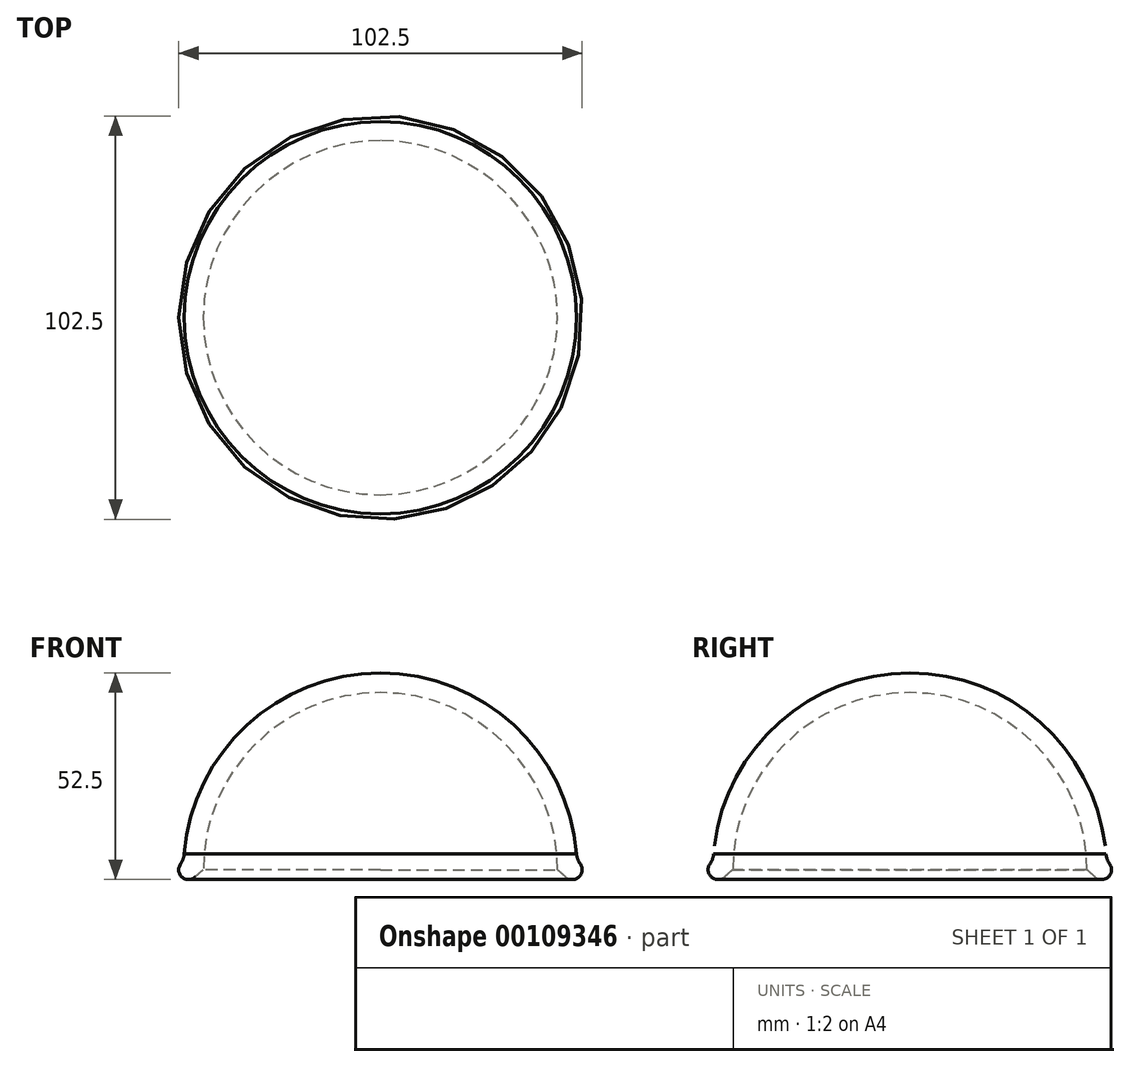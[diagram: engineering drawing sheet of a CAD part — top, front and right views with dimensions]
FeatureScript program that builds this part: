
annotation { "Feature Type Name" : "Feature", "Feature Type Description" : "" }
export const myFeature = defineFeature(function(context is Context, id is Id, definition is map)
    precondition{}
    {
        {
            var Q0;
            Q0=qCreatedBy(makeId("Top.planeOp"),FACE);
            var sketch = newSketch(context, id + "F0", { "sketchPlane" : qUnion([Q0])});
            skCircle(sketch, "E0", {"center": v(0, 0) * mm, "radius": 50 * mm});
            skLineSegment(sketch, "E1", {"start": v(0, -50) * mm, "end": v(0, 50) * mm});
            skSolve(sketch);
        }
        {
            var Q0;
            {var subQ0=sQuery(id+"F0.wireOp",EDGE,"E1");Q0=makeQuery(id+"F0.imprint","IMPRINT",FACE,{"disambiguationData":[TD([[makeQuery(id+"F0.imprint","IMPRINT",EDGE,{"derivedFrom":subQ0}),1.0]])]});}
            var Q1;
            Q1=sQuery(id+"F0.wireOp",EDGE,"E1");
            revolve(context, id + "F1", {"entities" : qUnion([Q0]), "axis" : qUnion([Q1]), "revolveType" : RevolveType.ONE_DIRECTION, "angle" : 180 * degree});
        }
        {
            var Q0;
            Q0=makeQuery(id+"F1.opRevolve","CAP_FACE",FACE,{"disambiguationData":[OSD([sQuery(id+"F0.wireOp",EDGE,"E0"),sQuery(id+"F0.wireOp",EDGE,"E1")])],"isStart":false});
            shell(context, id + "F2", {"entities" : qUnion([Q0]), "thickness" : 5 * mm});
        }
        {
            var Q0;
            Q0=qCreatedBy(makeId("Right.planeOp"),FACE);
            var sketch = newSketch(context, id + "F3", { "sketchPlane" : qUnion([Q0])});
            skCircle(sketch, "E2", {"center": v(-48.75, 0) * mm, "radius": 2.5 * mm});
            skSolve(sketch);
        }
        {
            var Q0;
            Q0=makeQuery(id+"F3.imprint","IMPRINT",FACE,{"disambiguationData":[TD([[makeQuery(id+"F3.imprint","IMPRINT",EDGE,{"derivedFrom":sQuery(id+"F3.wireOp",EDGE,"E2")}),1.0]])]});
            var Q1;
            Q1=makeQuery(id+"F2.opShell","OFFSET_EDGE",EDGE,{"disambiguationData":[OSD([sQuery(id+"F0.wireOp",EDGE,"E0")])]});
            sweep(context, id + "F4", {"operationType" : NewBodyOperationType.ADD, "profiles" : qUnion([Q0]), "path" : qUnion([Q1])});
        }
        {
            var Q0;
            {var subQ0=sQuery(id+"F0.wireOp",EDGE,"E0");Q0=makeQuery(id+"F4.boolean.opBoolean","INTERSECT",EDGE,{"derivedFrom":[makeQuery(id+"F1.opRevolve","SWEPT_FACE",FACE,{"disambiguationData":[OSD([subQ0])]}),makeQuery(id+"F4.opSweep","SWEPT_FACE",FACE,{"disambiguationData":[OSD([subQ0,sQuery(id+"F3.wireOp",EDGE,"E2")])]})]});}
            fillet(context, id + "F5", {"entities" : qUnion([Q0]), "radius" : 5 * mm, "tangentPropagation" : true, "allowEdgeOverflow" : false});
        }
        {
            var Q0;
            {var subQ0=sQuery(id+"F0.wireOp",EDGE,"E0");Q0=makeQuery(id+"F4.boolean.opBoolean","INTERSECT",EDGE,{"derivedFrom":[makeQuery(id+"F1.opRevolve","CAP_FACE",FACE,{"disambiguationData":[OSD([subQ0,sQuery(id+"F0.wireOp",EDGE,"E1")])],"isStart":false}),makeQuery(id+"F4.opSweep","SWEPT_FACE",FACE,{"disambiguationData":[OSD([subQ0,sQuery(id+"F3.wireOp",EDGE,"E2")])]})]});}
            fillet(context, id + "F6", {"entities" : qUnion([Q0]), "radius" : 30 * mm, "tangentPropagation" : true, "allowEdgeOverflow" : false});
        }
    });
